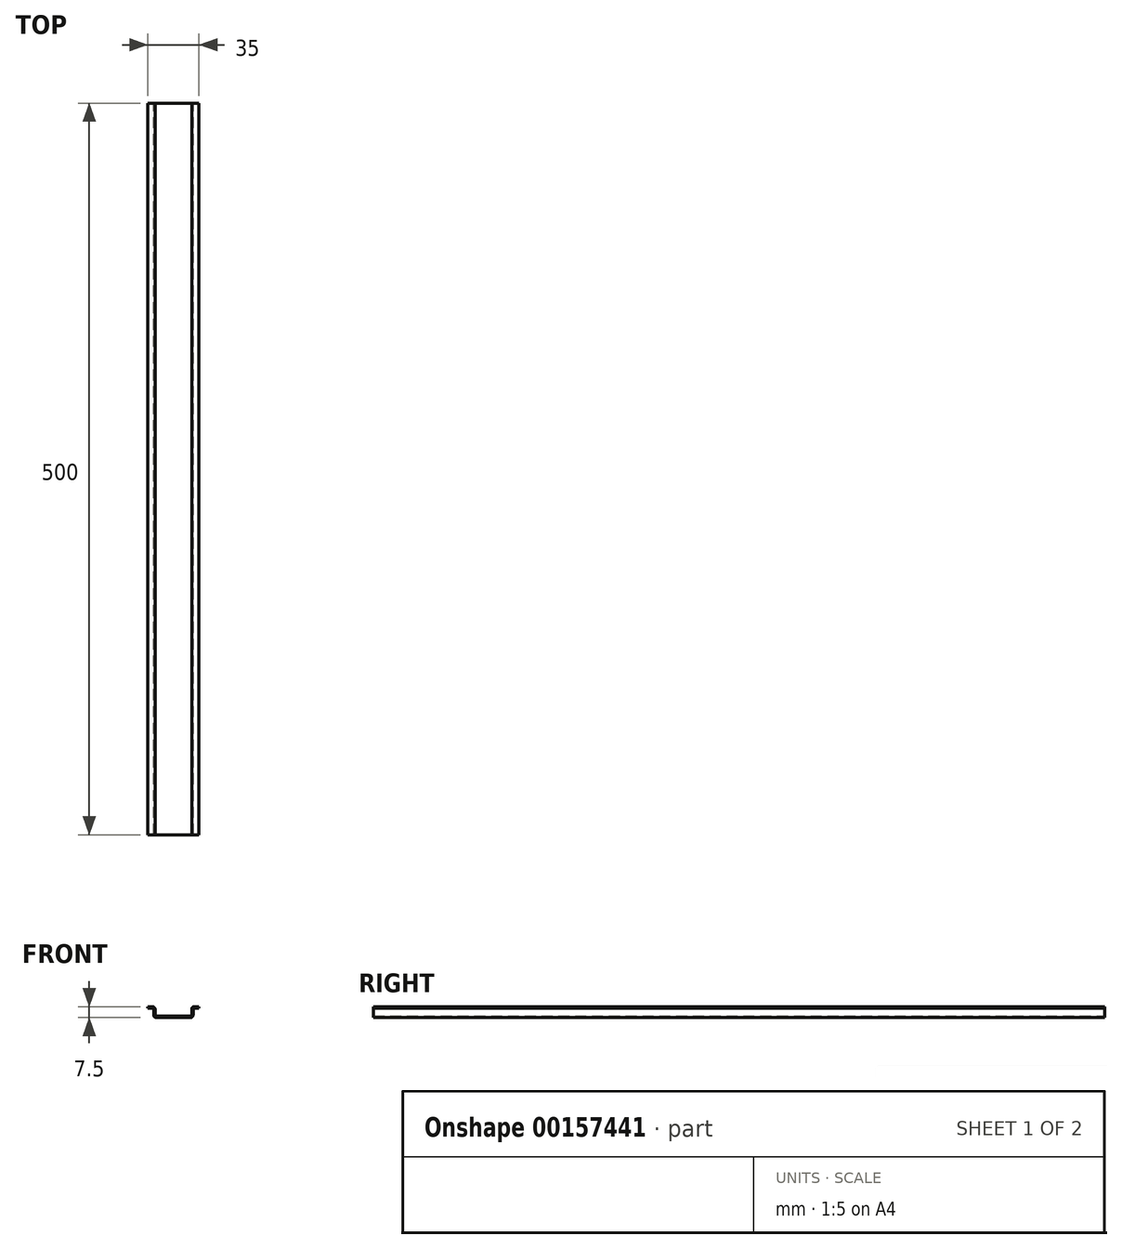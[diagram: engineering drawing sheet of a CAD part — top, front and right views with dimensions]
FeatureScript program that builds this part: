
annotation { "Feature Type Name" : "Feature", "Feature Type Description" : "" }
export const myFeature = defineFeature(function(context is Context, id is Id, definition is map)
    precondition{}
    {
        {
            var Q0;
            Q0=qCreatedBy(makeId("Front.planeOp"),FACE);
            var sketch = newSketch(context, id + "F0", { "sketchPlane" : qUnion([Q0])});
            skLineSegment(sketch, "E0", {"start": v(0, 0) * mm, "end": v(-23.4, 0) * mm});
            skArc(sketch, "E1", {"start": v(0, 0) * mm, "mid": v(1.27, 0.53) * mm, "end": v(1.8, 1.8) * mm});
            skArc(sketch, "E2", {"start": v(-23.4, 0) * mm, "mid": v(-24.67, 0.53) * mm, "end": v(-25.2, 1.8) * mm});
            skLineSegment(sketch, "E3", {"start": v(-25.2, 1.8) * mm, "end": v(-25.2, 5.7) * mm});
            skLineSegment(sketch, "E4", {"start": v(1.8, 1.8) * mm, "end": v(1.8, 5.7) * mm});
            skArc(sketch, "E5", {"start": v(-25.2, 5.7) * mm, "mid": v(-25.43, 6.27) * mm, "end": v(-26, 6.5) * mm});
            skArc(sketch, "E6", {"start": v(1.8, 5.7) * mm, "mid": v(2.03, 6.27) * mm, "end": v(2.6, 6.5) * mm});
            skLineSegment(sketch, "E7", {"start": v(-26, 6.5) * mm, "end": v(-29.2, 6.5) * mm});
            skLineSegment(sketch, "E8", {"start": v(2.6, 6.5) * mm, "end": v(5.8, 6.5) * mm});
            skLineSegment(sketch, "E9.0", {"start": v(-26, 7.5) * mm, "end": v(-29.2, 7.5) * mm});
            skArc(sketch, "E9.1", {"start": v(-24.2, 5.7) * mm, "mid": v(-24.73, 6.97) * mm, "end": v(-26, 7.5) * mm});
            skLineSegment(sketch, "E9.2", {"start": v(-24.2, 1.8) * mm, "end": v(-24.2, 5.7) * mm});
            skArc(sketch, "E9.3", {"start": v(-23.4, 1) * mm, "mid": v(-23.97, 1.23) * mm, "end": v(-24.2, 1.8) * mm});
            skLineSegment(sketch, "E9.4", {"start": v(0, 1) * mm, "end": v(-23.4, 1) * mm});
            skLineSegment(sketch, "E9.5", {"start": v(2.6, 7.5) * mm, "end": v(5.8, 7.5) * mm});
            skArc(sketch, "E9.6", {"start": v(0.8, 5.7) * mm, "mid": v(1.33, 6.97) * mm, "end": v(2.6, 7.5) * mm});
            skLineSegment(sketch, "E9.7", {"start": v(0.8, 1.8) * mm, "end": v(0.8, 5.7) * mm});
            skArc(sketch, "E9.8", {"start": v(0, 1) * mm, "mid": v(0.57, 1.23) * mm, "end": v(0.8, 1.8) * mm});
            skLineSegment(sketch, "E10", {"start": v(-29.2, 7.5) * mm, "end": v(-29.2, 6.5) * mm});
            skLineSegment(sketch, "E11", {"start": v(5.8, 7.5) * mm, "end": v(5.8, 6.5) * mm});
            skSolve(sketch);
        }
        {
            var Q0;
            Q0=makeQuery(id+"F0.imprint","IMPRINT",FACE,{"disambiguationData":[TD([[makeQuery(id+"F0.imprint","IMPRINT",EDGE,{"derivedFrom":sQuery(id+"F0.wireOp",EDGE,"E0")}),-1.0]])]});
            extrude(context, id + "F1", {"entities" : qUnion([Q0]), "depth" : 500 * mm});
        }
    });
